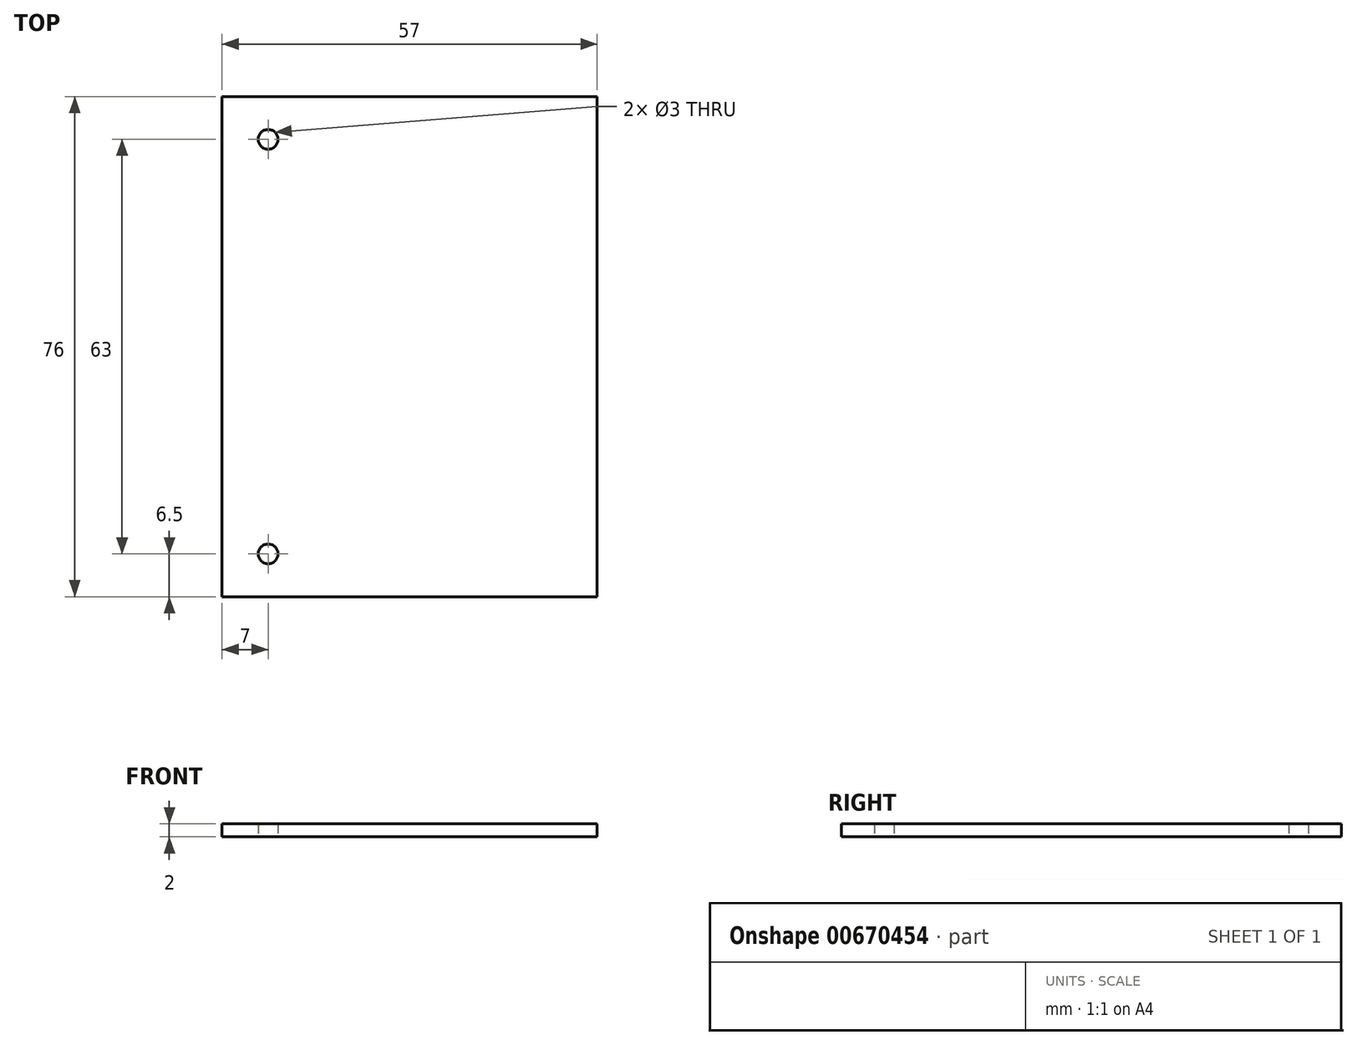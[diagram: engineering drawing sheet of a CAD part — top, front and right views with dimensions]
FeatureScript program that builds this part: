
annotation { "Feature Type Name" : "Feature", "Feature Type Description" : "" }
export const myFeature = defineFeature(function(context is Context, id is Id, definition is map)
    precondition{}
    {
        {
            var Q0;
            Q0=qCreatedBy(makeId("Top.planeOp"),FACE);
            var sketch = newSketch(context, id + "F0", { "sketchPlane" : qUnion([Q0])});
            skLineSegment(sketch, "E0.bottom", {"start": v(28.5, -38) * mm, "end": v(-28.5, -38) * mm});
            skLineSegment(sketch, "E0.top", {"start": v(28.5, 38) * mm, "end": v(-28.5, 38) * mm});
            skLineSegment(sketch, "E0.left", {"start": v(28.5, -38) * mm, "end": v(28.5, 38) * mm});
            skLineSegment(sketch, "E0.right", {"start": v(-28.5, -38) * mm, "end": v(-28.5, 38) * mm});
            skPoint(sketch, "E0.middle", {"position": v(0, 0) * mm});
            skCircle(sketch, "E1", {"center": v(-21.5, -31.5) * mm, "radius": 1.5 * mm});
            skCircle(sketch, "E2", {"center": v(-21.5, 31.5) * mm, "radius": 1.5 * mm});
            skSolve(sketch);
        }
        {
            var Q0;
            Q0 = qSketchRegion(id + "F0", true);
            extrude(context, id + "F1", {"entities" : qUnion([Q0]), "depth" : 2 * mm, "offsetDistance" : 25 * mm});
        }
    });
